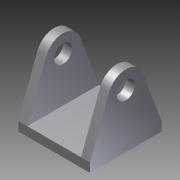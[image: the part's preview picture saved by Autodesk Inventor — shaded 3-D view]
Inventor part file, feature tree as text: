
AUTODESK INVENTOR PART (.ipt)
format: ipt  version: 2012 (Build 160160000, 160)  size: 110,080 bytes
history: native  units: in
note: dims shown in document units (in); Inventor stores cm internally (conversion verified against a paired STEP export)
features: extrude x2, sketch x2
ambient origin geometry x8: Origin, YZ Plane, XZ Plane, XY Plane, X Axis, Y Axis, Z Axis, Center Point
bodies: Solid1 (feature_tree)
feature tree (4):
  extrude  "Extrusion1"  Depth=1.0in
  extrude  "Extrusion2"  Depth=0.125in
  sketch  "Sketch1"  dims[d0=1.0in d1=1.0in]
  sketch  "Sketch2"  dims[d2=0.125in d3=0.125in d4=0.125in d5=1.0in d6=0.0in d7=0.75in d8=0.5in d9=0.25in d10=0.125in d11=0.125in d12=1.0in d13=0.0in]
